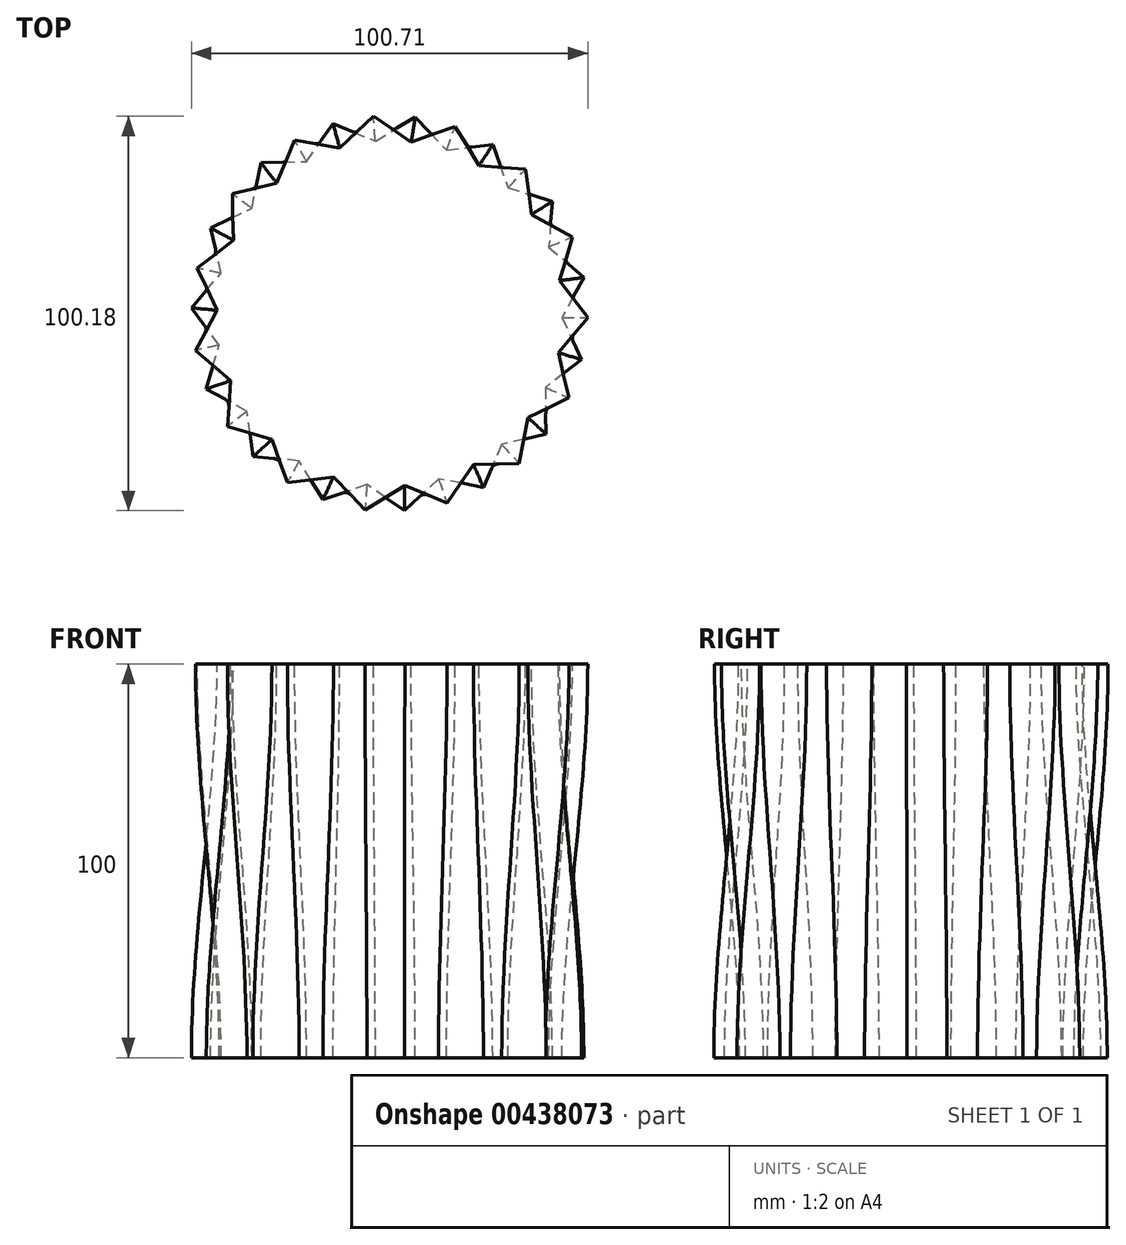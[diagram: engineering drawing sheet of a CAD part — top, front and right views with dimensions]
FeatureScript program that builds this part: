
annotation { "Feature Type Name" : "Feature", "Feature Type Description" : "" }
export const myFeature = defineFeature(function(context is Context, id is Id, definition is map)
    precondition{}
    {
        {
            var Q0;
            Q0=qCreatedBy(makeId("Top.planeOp"),FACE);
            var sketch = newSketch(context, id + "F0", { "sketchPlane" : qUnion([Q0])});
            skLineSegment(sketch, "E0", {"start": v(24.35, -44.06) * mm, "end": v(12.95, -41.94) * mm});
            skLineSegment(sketch, "E1", {"start": v(12.95, -41.94) * mm, "end": v(4.3, -49.98) * mm});
            skLineSegment(sketch, "E2", {"start": v(4.3, -49.98) * mm, "end": v(-5.25, -43.4) * mm});
            skLineSegment(sketch, "E3", {"start": v(-5.25, -43.4) * mm, "end": v(-16.42, -47.23) * mm});
            skLineSegment(sketch, "E4", {"start": v(-16.42, -47.23) * mm, "end": v(-22.47, -37.34) * mm});
            skLineSegment(sketch, "E5", {"start": v(-22.47, -37.34) * mm, "end": v(-34.24, -36.3) * mm});
            skLineSegment(sketch, "E6", {"start": v(-34.24, -36.3) * mm, "end": v(-35.74, -24.8) * mm});
            skLineSegment(sketch, "E7", {"start": v(-35.74, -24.8) * mm, "end": v(-46.06, -19.05) * mm});
            skLineSegment(sketch, "E8", {"start": v(-46.06, -19.05) * mm, "end": v(-42.75, -7.93) * mm});
            skLineSegment(sketch, "E9", {"start": v(-42.75, -7.93) * mm, "end": v(-49.85, 1.5) * mm});
            skLineSegment(sketch, "E10", {"start": v(-49.85, 1.5) * mm, "end": v(-42.3, 10.32) * mm});
            skLineSegment(sketch, "E11", {"start": v(-42.3, 10.32) * mm, "end": v(-44.95, 21.83) * mm});
            skLineSegment(sketch, "E12", {"start": v(-44.95, 21.83) * mm, "end": v(-34.48, 26.81) * mm});
            skLineSegment(sketch, "E13", {"start": v(-34.48, 26.81) * mm, "end": v(-32.2, 38.4) * mm});
            skLineSegment(sketch, "E14", {"start": v(-32.2, 38.4) * mm, "end": v(-20.61, 38.7) * mm});
            skLineSegment(sketch, "E15", {"start": v(-20.61, 38.7) * mm, "end": v(-13.82, 48.36) * mm});
            skLineSegment(sketch, "E16", {"start": v(-13.82, 48.36) * mm, "end": v(-3.11, 43.91) * mm});
            skLineSegment(sketch, "E17", {"start": v(-3.11, 43.91) * mm, "end": v(7.02, 49.98) * mm});
            skLineSegment(sketch, "E18", {"start": v(7.02, 49.98) * mm, "end": v(15, 41.56) * mm});
            skLineSegment(sketch, "E19", {"start": v(15, 41.56) * mm, "end": v(26.72, 42.98) * mm});
            skLineSegment(sketch, "E20", {"start": v(26.72, 42.98) * mm, "end": v(30.58, 32.05) * mm});
            skLineSegment(sketch, "E21", {"start": v(30.58, 32.05) * mm, "end": v(41.87, 28.58) * mm});
            skLineSegment(sketch, "E22", {"start": v(41.87, 28.58) * mm, "end": v(40.94, 17.02) * mm});
            skLineSegment(sketch, "E23", {"start": v(40.94, 17.02) * mm, "end": v(49.85, 9.26) * mm});
            skLineSegment(sketch, "E24", {"start": v(49.85, 9.26) * mm, "end": v(44.3, -0.93) * mm});
            skLineSegment(sketch, "E25", {"start": v(44.3, -0.93) * mm, "end": v(49.28, -11.64) * mm});
            skLineSegment(sketch, "E26", {"start": v(49.28, -11.64) * mm, "end": v(40.07, -18.7) * mm});
            skLineSegment(sketch, "E27", {"start": v(40.07, -18.7) * mm, "end": v(40.26, -30.5) * mm});
            skLineSegment(sketch, "E28", {"start": v(40.26, -30.5) * mm, "end": v(28.98, -33.2) * mm});
            skLineSegment(sketch, "E29", {"start": v(28.98, -33.2) * mm, "end": v(24.35, -44.06) * mm});
            skLineSegment(sketch, "E30", {"start": v(-42.3, 10.32) * mm, "end": v(49.28, -11.64) * mm, "construction": true});
            skCircle(sketch, "E31", {"center": v(0, 0) * mm, "radius": 50.47 * mm, "construction": true});
            skSolve(sketch);
        }
        {
            var Q0;
            Q0=qCreatedBy(makeId("Top.planeOp"),FACE);
            cPlane(context, id + "F1", {"entities" : qUnion([Q0]), "cplaneType" : CPlaneType.OFFSET, "offset" : 100 * mm, "width" : 150 * mm, "height" : 150 * mm});
        }
        {
            var Q0;
            Q0=qCreatedBy(id+"F1.planeOp",FACE);
            var sketch = newSketch(context, id + "F2", { "sketchPlane" : qUnion([Q0])});
            skLineSegment(sketch, "E32", {"start": v(33.43, -37.97) * mm, "end": v(21.84, -38.33) * mm});
            skLineSegment(sketch, "E33", {"start": v(21.84, -38.33) * mm, "end": v(15.1, -48.03) * mm});
            skLineSegment(sketch, "E34", {"start": v(15.1, -48.03) * mm, "end": v(4.37, -43.64) * mm});
            skLineSegment(sketch, "E35", {"start": v(4.37, -43.64) * mm, "end": v(-5.73, -49.77) * mm});
            skLineSegment(sketch, "E36", {"start": v(-5.73, -49.77) * mm, "end": v(-13.75, -41.4) * mm});
            skLineSegment(sketch, "E37", {"start": v(-13.75, -41.4) * mm, "end": v(-25.47, -42.9) * mm});
            skLineSegment(sketch, "E38", {"start": v(-25.47, -42.9) * mm, "end": v(-29.4, -31.98) * mm});
            skLineSegment(sketch, "E39", {"start": v(-29.4, -31.98) * mm, "end": v(-40.7, -28.57) * mm});
            skLineSegment(sketch, "E40", {"start": v(-40.7, -28.57) * mm, "end": v(-39.85, -17) * mm});
            skLineSegment(sketch, "E41", {"start": v(-39.85, -17) * mm, "end": v(-48.8, -9.3) * mm});
            skLineSegment(sketch, "E42", {"start": v(-43.3, 0.92) * mm, "end": v(-48.35, 11.6) * mm});
            skLineSegment(sketch, "E43", {"start": v(-48.35, 11.6) * mm, "end": v(-39.18, 18.7) * mm});
            skLineSegment(sketch, "E44", {"start": v(-39.18, 18.7) * mm, "end": v(-39.44, 30.52) * mm});
            skLineSegment(sketch, "E45", {"start": v(-39.44, 30.52) * mm, "end": v(-28.18, 33.27) * mm});
            skLineSegment(sketch, "E46", {"start": v(-28.18, 33.27) * mm, "end": v(-23.6, 44.17) * mm});
            skLineSegment(sketch, "E47", {"start": v(-23.6, 44.17) * mm, "end": v(-12.2, 42.1) * mm});
            skLineSegment(sketch, "E48", {"start": v(-3.6, 50.2) * mm, "end": v(6, 43.68) * mm});
            skLineSegment(sketch, "E49", {"start": v(6, 43.68) * mm, "end": v(17.15, 47.57) * mm});
            skLineSegment(sketch, "E50", {"start": v(17.15, 47.57) * mm, "end": v(23.25, 37.71) * mm});
            skLineSegment(sketch, "E51", {"start": v(23.25, 37.71) * mm, "end": v(35.02, 36.74) * mm});
            skLineSegment(sketch, "E52", {"start": v(35.02, 36.74) * mm, "end": v(36.6, 25.25) * mm});
            skLineSegment(sketch, "E53", {"start": v(36.6, 25.25) * mm, "end": v(46.95, 19.57) * mm});
            skLineSegment(sketch, "E54", {"start": v(46.95, 19.57) * mm, "end": v(43.7, 8.43) * mm});
            skLineSegment(sketch, "E55", {"start": v(50.86, -0.97) * mm, "end": v(43.37, -9.82) * mm});
            skLineSegment(sketch, "E56", {"start": v(43.37, -9.82) * mm, "end": v(46.07, -21.32) * mm});
            skLineSegment(sketch, "E57", {"start": v(46.07, -21.32) * mm, "end": v(35.63, -26.36) * mm});
            skLineSegment(sketch, "E58", {"start": v(35.63, -26.36) * mm, "end": v(33.43, -37.97) * mm});
            skLineSegment(sketch, "E59", {"start": v(-43.3, 0.92) * mm, "end": v(50.86, -0.97) * mm, "construction": true});
            skCircle(sketch, "E60", {"center": v(0.23, -0.12) * mm, "radius": 42.66 * mm, "construction": true});
            skLineSegment(sketch, "E61", {"start": v(-43.3, 0.92) * mm, "end": v(-48.8, -9.3) * mm});
            skLineSegment(sketch, "E62", {"start": v(-12.2, 42.1) * mm, "end": v(-3.6, 50.2) * mm});
            skLineSegment(sketch, "E63", {"start": v(43.7, 8.43) * mm, "end": v(50.86, -0.97) * mm});
            skSolve(sketch);
        }
        {
            var Q0;
            Q0=makeQuery(id+"F0.imprint","IMPRINT",FACE,{"disambiguationData":[TD([[makeQuery(id+"F0.imprint","IMPRINT",EDGE,{"derivedFrom":sQuery(id+"F0.wireOp",EDGE,"E0")}),-1.0]])]});
            var Q1;
            Q1=makeQuery(id+"F2.imprint","IMPRINT",FACE,{"disambiguationData":[TD([[makeQuery(id+"F2.imprint","IMPRINT",EDGE,{"derivedFrom":sQuery(id+"F2.wireOp",EDGE,"E32")}),-1.0]])]});
            loft(context, id + "F3", {"startCondition" : LoftEndDerivativeType.NORMAL_TO_PROFILE, "startMagnitude" : 1, "endCondition" : LoftEndDerivativeType.NORMAL_TO_PROFILE, "endMagnitude" : 1, "sheetProfilesArray" : [{ "sheetProfileEntities" : qUnion([Q0]) }, { "sheetProfileEntities" : qUnion([Q1]) }]});
        }
    });
